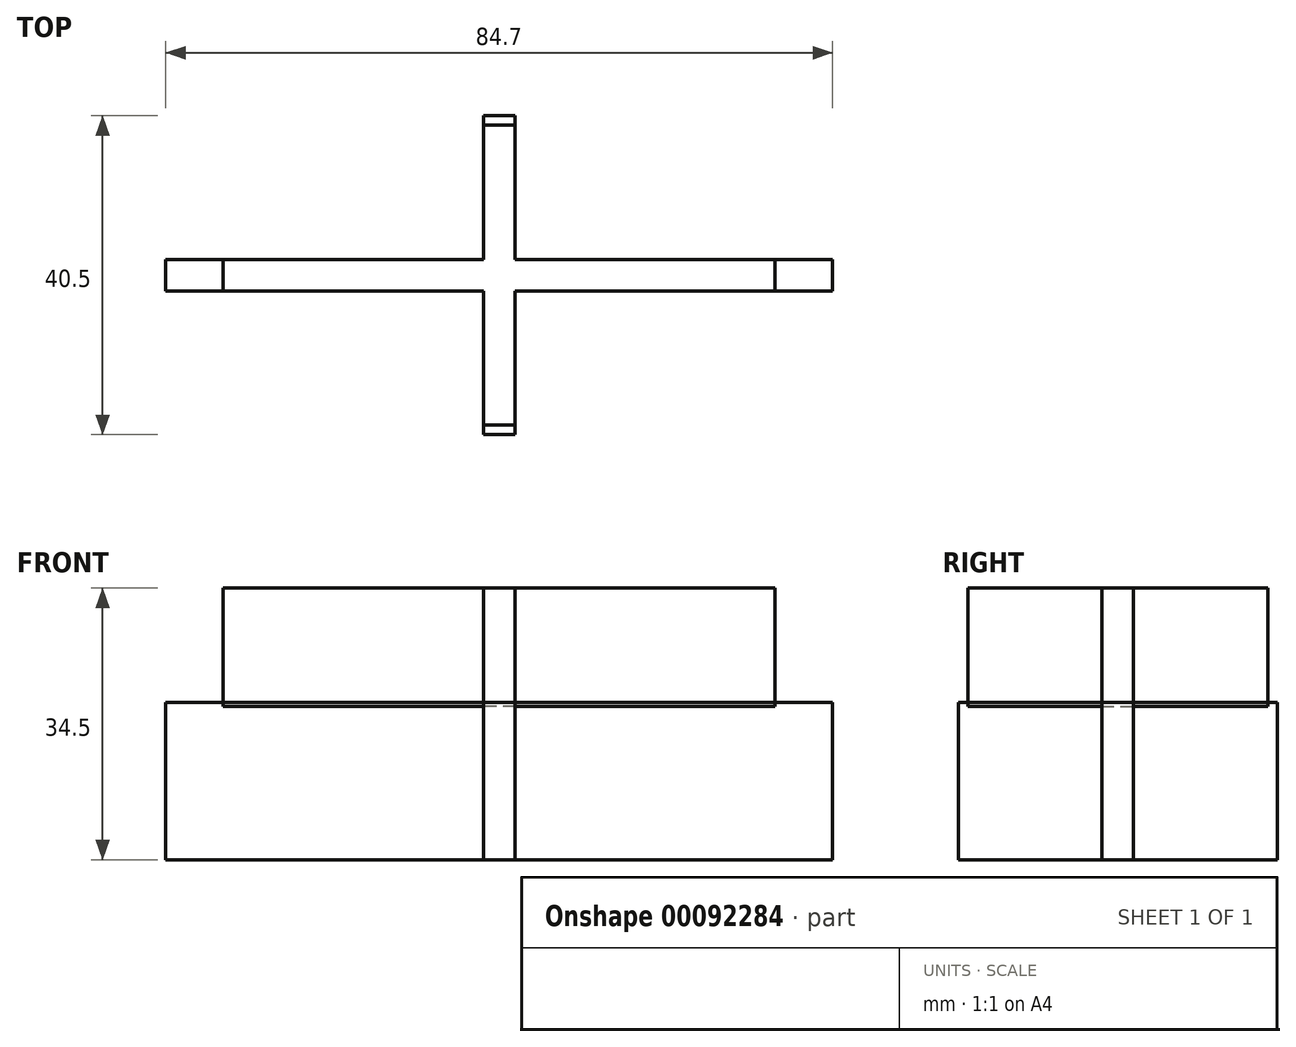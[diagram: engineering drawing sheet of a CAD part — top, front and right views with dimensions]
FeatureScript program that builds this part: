
annotation { "Feature Type Name" : "Feature", "Feature Type Description" : "" }
export const myFeature = defineFeature(function(context is Context, id is Id, definition is map)
    precondition{}
    {
        {
            var Q0;
            Q0=qCreatedBy(makeId("Top.planeOp"),FACE);
            var sketch = newSketch(context, id + "F0", { "sketchPlane" : qUnion([Q0])});
            skLineSegment(sketch, "E0", {"start": v(-101.3, 5.7) * mm, "end": v(-60.96, 5.7) * mm});
            skLineSegment(sketch, "E1", {"start": v(-60.96, 5.7) * mm, "end": v(-60.96, 23.94) * mm});
            skLineSegment(sketch, "E2", {"start": v(-60.96, 23.94) * mm, "end": v(-56.96, 23.94) * mm});
            skLineSegment(sketch, "E3", {"start": v(-56.96, 23.94) * mm, "end": v(-56.96, 5.7) * mm});
            skLineSegment(sketch, "E4", {"start": v(-56.96, 5.7) * mm, "end": v(-16.6, 5.7) * mm});
            skLineSegment(sketch, "E5", {"start": v(-16.6, 5.7) * mm, "end": v(-16.6, 1.7) * mm});
            skLineSegment(sketch, "E6", {"start": v(-16.6, 1.7) * mm, "end": v(-56.96, 1.7) * mm});
            skLineSegment(sketch, "E7", {"start": v(-56.96, 1.7) * mm, "end": v(-56.96, -16.56) * mm});
            skLineSegment(sketch, "E8", {"start": v(-56.96, -16.56) * mm, "end": v(-60.96, -16.56) * mm});
            skLineSegment(sketch, "E9", {"start": v(-60.96, -16.56) * mm, "end": v(-60.96, 1.7) * mm});
            skLineSegment(sketch, "E10", {"start": v(-60.96, 1.7) * mm, "end": v(-101.3, 1.7) * mm});
            skLineSegment(sketch, "E11", {"start": v(-101.3, 1.7) * mm, "end": v(-101.3, 5.7) * mm});
            skSolve(sketch);
        }
        {
            var Q0;
            Q0=makeQuery(id+"F0.imprint","IMPRINT",FACE,{"disambiguationData":[TD([[makeQuery(id+"F0.imprint","IMPRINT",EDGE,{"derivedFrom":sQuery(id+"F0.wireOp",EDGE,"E0")}),-1.0]])]});
            extrude(context, id + "F1", {"entities" : qUnion([Q0]), "depth" : 20 * mm});
        }
        {
            var Q0;
            Q0=qCreatedBy(makeId("Top.planeOp"),FACE);
            var sketch = newSketch(context, id + "F2", { "sketchPlane" : qUnion([Q0])});
            skLineSegment(sketch, "E12", {"start": v(-2.96, -0.91) * mm, "end": v(-2.96, 3.09) * mm});
            skLineSegment(sketch, "E13", {"start": v(-2.96, 3.09) * mm, "end": v(30.09, 3.09) * mm});
            skLineSegment(sketch, "E14", {"start": v(30.09, 3.09) * mm, "end": v(30.09, 20.14) * mm});
            skLineSegment(sketch, "E15", {"start": v(30.09, 20.14) * mm, "end": v(34.09, 20.14) * mm});
            skLineSegment(sketch, "E16", {"start": v(34.09, 20.14) * mm, "end": v(34.09, 3.09) * mm});
            skLineSegment(sketch, "E17", {"start": v(34.09, 3.09) * mm, "end": v(67.14, 3.09) * mm});
            skLineSegment(sketch, "E18", {"start": v(67.14, 3.09) * mm, "end": v(67.14, -0.91) * mm});
            skLineSegment(sketch, "E19", {"start": v(67.14, -0.91) * mm, "end": v(34.09, -0.91) * mm});
            skLineSegment(sketch, "E20", {"start": v(34.09, -0.91) * mm, "end": v(34.09, -17.96) * mm});
            skLineSegment(sketch, "E21", {"start": v(34.09, -17.96) * mm, "end": v(30.09, -17.96) * mm});
            skLineSegment(sketch, "E22", {"start": v(30.09, -17.96) * mm, "end": v(30.09, -0.91) * mm});
            skLineSegment(sketch, "E23", {"start": v(30.09, -0.91) * mm, "end": v(-2.96, -0.91) * mm});
            skSolve(sketch);
        }
        {
            var Q0;
            Q0=makeQuery(id+"F2.imprint","IMPRINT",FACE,{"disambiguationData":[TD([[makeQuery(id+"F2.imprint","IMPRINT",EDGE,{"derivedFrom":sQuery(id+"F2.wireOp",EDGE,"E12")}),-1.0]])]});
            extrude(context, id + "F3", {"entities" : qUnion([Q0]), "depth" : 15 * mm});
        }
        {
            var Q0;
            Q0=makeQuery(id+"F3.opExtrude","SWEPT_BODY",BODY,{"disambiguationData":[OSD([sQuery(id+"F2.wireOp",EDGE,"E12"),sQuery(id+"F2.wireOp",EDGE,"E13"),sQuery(id+"F2.wireOp",EDGE,"E14"),sQuery(id+"F2.wireOp",EDGE,"E15"),sQuery(id+"F2.wireOp",EDGE,"E16"),sQuery(id+"F2.wireOp",EDGE,"E17"),sQuery(id+"F2.wireOp",EDGE,"E18"),sQuery(id+"F2.wireOp",EDGE,"E19"),sQuery(id+"F2.wireOp",EDGE,"E20"),sQuery(id+"F2.wireOp",EDGE,"E21"),sQuery(id+"F2.wireOp",EDGE,"E22"),sQuery(id+"F2.wireOp",EDGE,"E23")])]});
            transform(context, id + "F4", {"entities" : qUnion([Q0]), "transformType" : TransformType.TRANSLATION_3D, "dx" : -32.03 * mm, "dy" : -1.08 * mm, "dz" : 19.5 * mm, "makeCopy" : false});
        }
        {
            var Q0;
            Q0=makeQuery(id+"F1.opExtrude","SWEPT_BODY",BODY,{"disambiguationData":[OSD([sQuery(id+"F0.wireOp",EDGE,"E0"),sQuery(id+"F0.wireOp",EDGE,"E1"),sQuery(id+"F0.wireOp",EDGE,"E2"),sQuery(id+"F0.wireOp",EDGE,"E3"),sQuery(id+"F0.wireOp",EDGE,"E4"),sQuery(id+"F0.wireOp",EDGE,"E5"),sQuery(id+"F0.wireOp",EDGE,"E6"),sQuery(id+"F0.wireOp",EDGE,"E7"),sQuery(id+"F0.wireOp",EDGE,"E8"),sQuery(id+"F0.wireOp",EDGE,"E9"),sQuery(id+"F0.wireOp",EDGE,"E10"),sQuery(id+"F0.wireOp",EDGE,"E11")])]});
            transform(context, id + "F5", {"entities" : qUnion([Q0]), "transformType" : TransformType.TRANSLATION_3D, "dx" : 59.02 * mm, "dy" : -3.69 * mm, "dz" : 0 * mm, "makeCopy" : false});
        }
    });
